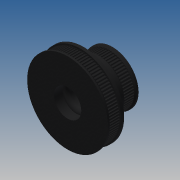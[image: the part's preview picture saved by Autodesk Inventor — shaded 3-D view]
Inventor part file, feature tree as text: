
AUTODESK INVENTOR PART (.ipt)
format: ipt  version: 2013 (Build 170138000, 138)  size: 900,608 bytes
history: native  units: mm
features: extrude x10, sketch x10, pattern_circular x2, chamfer x2, mirror x1, fillet x1
ambient origin geometry x8: Origin, YZ Plane, XZ Plane, XY Plane, X Axis, Y Axis, Z Axis, Center Point
bodies: Solid1 (feature_tree)
feature tree (26):
  extrude  "Extrusion1"  Depth=8.0mm TaperAngle=0.0deg
  extrude  "Extrusion2"  Depth=8.0mm TaperAngle=0.0deg
  pattern_circular  "Circular Pattern1"  Count=100 Angle=360.0deg
  extrude  "Extrusion3"  Depth=2.5mm TaperAngle=0.0deg
  chamfer  "Chamfer1"  Distance=1.0mm Angle=45.0deg
  mirror  "Mirror1"
  extrude  "Extrusion4"  Depth=23.1mm TaperAngle=0.0deg
  extrude  "Extrusion5"  Depth=23.1mm TaperAngle=0.0deg
  pattern_circular  "Circular Pattern2"  Count=64 Angle=360.0deg
  extrude  "Extrusion6"  Depth=12.6mm TaperAngle=0.0deg
  extrude  "Extrusion7"  Depth=1.0mm TaperAngle=45.0deg
  chamfer  "Chamfer2"  Distance=2.5mm
  extrude  "Extrusion8"  Depth=7.0mm TaperAngle=0.0deg
  extrude  "Extrusion9"  Depth=7.0mm TaperAngle=0.0deg
  extrude  "Extrusion10"  Depth=3.5mm
  fillet  "Fillet1"  [1 undecoded]
  sketch  "Sketch1"  dims[d0=63.153977mm d3=8.0mm d4=0.0mm]
  sketch  "Sketch2"  dims[d5=1.59mm d7=8.0mm d8=0.0mm d9=1000.0mm d10=360.0deg]
  sketch  "Sketch4"  dims[d12=1.0mm d13=2.5mm d14=0.0mm d15=1.0mm d16=2.0mm d17=45.0deg]
  sketch  "Sketch5"  dims[d18=40.235665mm d20=23.1mm d21=0.0mm]
  sketch  "Sketch6"  dims[d22=1.59mm d24=23.1mm d25=0.0mm d26=640.0mm d27=360.0deg]
  sketch  "Sketch7"  dims[d29=1.0mm d30=12.6mm d31=0.0mm]
  sketch  "Sketch8"  dims[d32=2.5mm d33=0.0mm d34=1.0mm d35=2.0mm d36=45.0deg]
  sketch  "Sketch9"  dims[d37=15.0mm d39=2.5mm d40=0.0mm]
  sketch  "Sketch10"  dims[d41=22.0mm d43=7.0mm d44=0.0mm]
  sketch  "Sketch11"  dims[d45=22.0mm d47=7.0mm d48=0.0mm d49=3.5mm]
note: 1 required parameter value undecoded (feature->parameter linkage not recoverable at this tier; creation-order binding heuristic only, values carry confidence <= 0.55)
